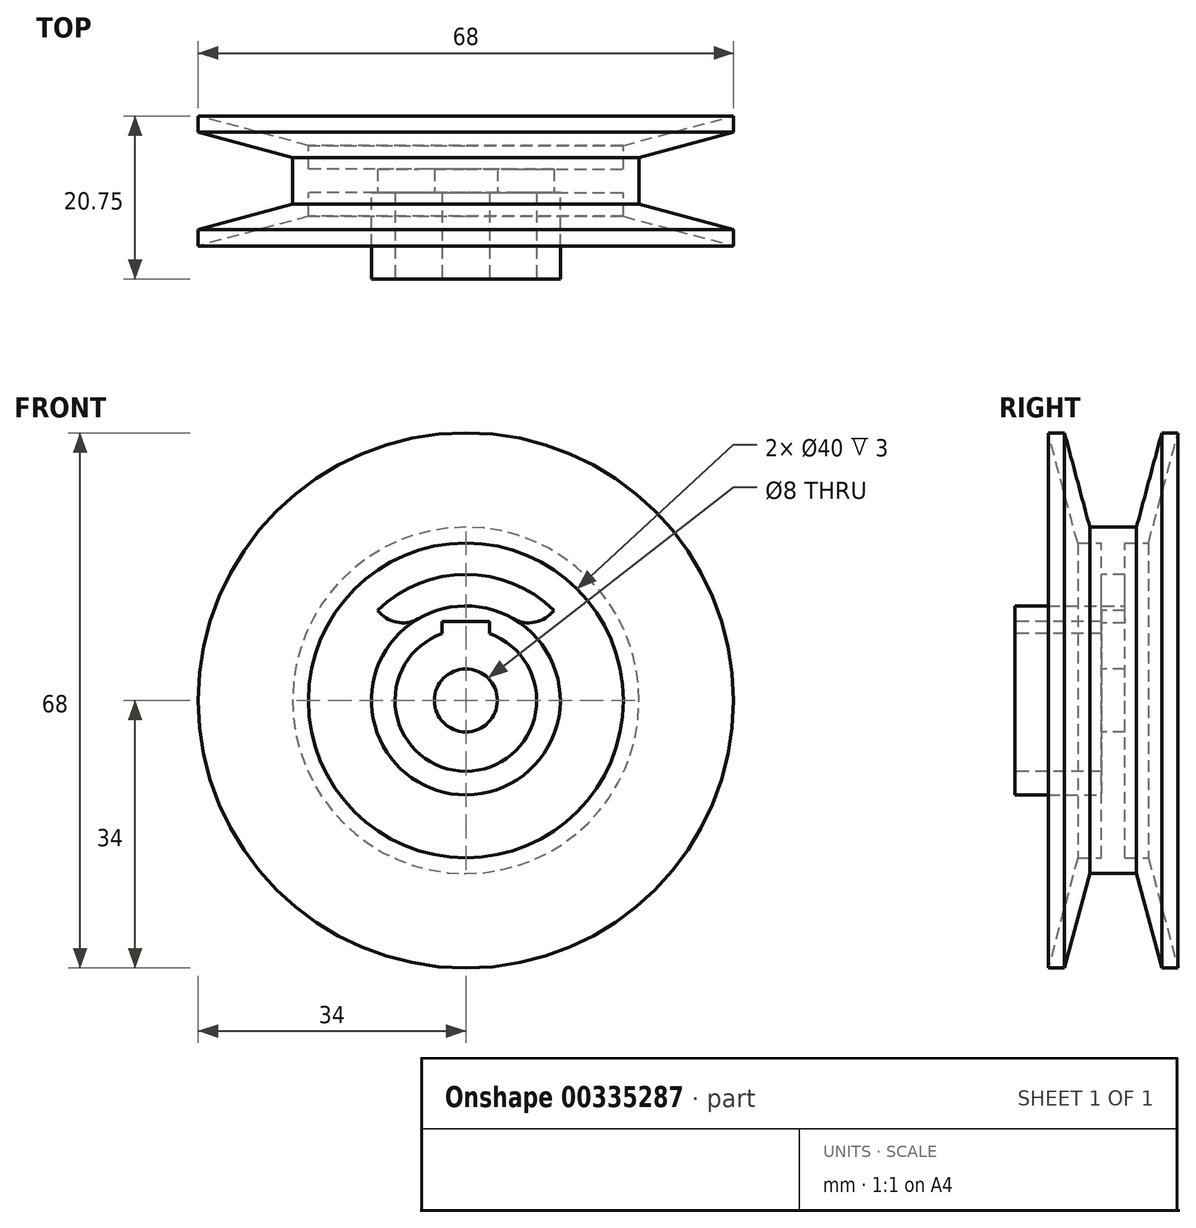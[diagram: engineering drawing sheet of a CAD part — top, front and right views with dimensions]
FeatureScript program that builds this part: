
annotation { "Feature Type Name" : "Feature", "Feature Type Description" : "" }
export const myFeature = defineFeature(function(context is Context, id is Id, definition is map)
    precondition{}
    {
        {
            var Q0;
            Q0=qCreatedBy(makeId("Front.planeOp"),FACE);
            var sketch = newSketch(context, id + "F0", { "sketchPlane" : qUnion([Q0])});
            skCircle(sketch, "E0", {"center": v(0, 0) * mm, "radius": 20 * mm});
            skSolve(sketch);
        }
        {
            var Q0;
            Q0=makeQuery(id+"F0.imprint","IMPRINT",FACE,{"disambiguationData":[TD([[makeQuery(id+"F0.imprint","IMPRINT",EDGE,{"derivedFrom":sQuery(id+"F0.wireOp",EDGE,"E0")}),1.0]])]});
            extrude(context, id + "F1", {"entities" : qUnion([Q0]), "depth" : 3 * mm, "symmetric" : true});
        }
        {
            var Q0;
            Q0=qCreatedBy(makeId("Right.planeOp"),FACE);
            var sketch = newSketch(context, id + "F2", { "sketchPlane" : qUnion([Q0])});
            skLineSegment(sketch, "E1", {"start": v(0, 20) * mm, "end": v(4.5, 20) * mm});
            skLineSegment(sketch, "E2", {"start": v(4.5, 20) * mm, "end": v(8.25, 34) * mm});
            skLineSegment(sketch, "E3.0", {"start": v(0, 22) * mm, "end": v(2.97, 22) * mm});
            skLineSegment(sketch, "E4.0", {"start": v(2.97, 22) * mm, "end": v(6.18, 34) * mm});
            skLineSegment(sketch, "E5", {"start": v(6.18, 34) * mm, "end": v(8.25, 34) * mm});
            skLineSegment(sketch, "E6", {"start": v(0, 20) * mm, "end": v(0, 22) * mm});
            skLineSegment(sketch, "E7.MirrorCS", {"start": v(0, 22) * mm, "end": v(-2.97, 22) * mm});
            skLineSegment(sketch, "E8.MirrorCS", {"start": v(-2.97, 22) * mm, "end": v(-6.18, 34) * mm});
            skLineSegment(sketch, "E9.MirrorCS", {"start": v(-6.18, 34) * mm, "end": v(-8.25, 34) * mm});
            skLineSegment(sketch, "E10.MirrorCS", {"start": v(-4.5, 20) * mm, "end": v(-8.25, 34) * mm});
            skLineSegment(sketch, "E11.MirrorCS", {"start": v(0, 20) * mm, "end": v(-4.5, 20) * mm});
            skSolve(sketch);
        }
        {
            var Q0;
            Q0 = qSketchRegion(id + "F2", true);
            var Q1;
            Q1=makeQuery(id+"F1.opExtrude","CAP_EDGE",EDGE,{"disambiguationData":[OSD([sQuery(id+"F0.wireOp",EDGE,"E0")])],"isStart":false});
            revolve(context, id + "F3", {"operationType" : NewBodyOperationType.ADD, "entities" : qUnion([Q0]), "axis" : qUnion([Q1]), "revolveType" : RevolveType.FULL});
        }
        {
            var Q0;
            Q0=makeQuery(id+"F1.opExtrude","CAP_FACE",FACE,{"disambiguationData":[OSD([sQuery(id+"F0.wireOp",EDGE,"E0")])],"isStart":false});
            var sketch = newSketch(context, id + "F4", { "sketchPlane" : qUnion([Q0])});
            skCircle(sketch, "E12", {"center": v(0, 0) * mm, "radius": 12 * mm});
            skSolve(sketch);
        }
        {
            var Q0;
            Q0=makeQuery(id+"F4.imprint","IMPRINT",FACE,{"disambiguationData":[TD([[makeQuery(id+"F4.imprint","IMPRINT",EDGE,{"derivedFrom":sQuery(id+"F4.wireOp",EDGE,"E12")}),1.0]])]});
            extrude(context, id + "F5", {"entities" : qUnion([Q0]), "operationType" : NewBodyOperationType.ADD, "depth" : 11 * mm});
        }
        {
            var Q0;
            Q0=makeQuery(id+"F5.opExtrude","CAP_FACE",FACE,{"disambiguationData":[OSD([sQuery(id+"F4.wireOp",EDGE,"E12")])],"isStart":false});
            var sketch = newSketch(context, id + "F6", { "sketchPlane" : qUnion([Q0])});
            skCircle(sketch, "E13", {"center": v(0, 0) * mm, "radius": 9 * mm});
            skSolve(sketch);
        }
        {
            var Q0;
            Q0=makeQuery(id+"F6.imprint","IMPRINT",FACE,{"disambiguationData":[TD([[makeQuery(id+"F6.imprint","IMPRINT",EDGE,{"derivedFrom":sQuery(id+"F6.wireOp",EDGE,"E13")}),1.0]])]});
            extrude(context, id + "F7", {"entities" : qUnion([Q0]), "operationType" : NewBodyOperationType.REMOVE, "oppositeDirection" : true, "depth" : 11 * mm});
        }
        {
            var Q0;
            Q0=makeQuery(id+"F7.boolean.opBoolean","COPY",FACE,{"derivedFrom":makeQuery(id+"F7.opExtrude","CAP_FACE",FACE,{"disambiguationData":[OSD([sQuery(id+"F6.wireOp",EDGE,"E13")])],"isStart":false})});
            var sketch = newSketch(context, id + "F8", { "sketchPlane" : qUnion([Q0])});
            skCircle(sketch, "E14", {"center": v(0, 0) * mm, "radius": 4 * mm});
            skSolve(sketch);
        }
        {
            var Q0;
            Q0=makeQuery(id+"F8.imprint","IMPRINT",FACE,{"disambiguationData":[TD([[makeQuery(id+"F8.imprint","IMPRINT",EDGE,{"derivedFrom":sQuery(id+"F8.wireOp",EDGE,"E14")}),1.0]])]});
            extrude(context, id + "F9", {"entities" : qUnion([Q0]), "operationType" : NewBodyOperationType.REMOVE, "oppositeDirection" : true, "depth" : 25 * mm});
        }
        {
            var Q0;
            Q0=makeQuery(id+"F5.opExtrude","CAP_FACE",FACE,{"disambiguationData":[OSD([sQuery(id+"F4.wireOp",EDGE,"E12")])],"isStart":false});
            var sketch = newSketch(context, id + "F10", { "sketchPlane" : qUnion([Q0])});
            skCircle(sketch, "E15.0", {"center": v(0, 0) * mm, "radius": 9 * mm});
            skLineSegment(sketch, "E16.bottom", {"start": v(3, 10) * mm, "end": v(-3, 10) * mm});
            skLineSegment(sketch, "E16.top", {"start": v(3, 8.49) * mm, "end": v(-3, 8.49) * mm});
            skLineSegment(sketch, "E16.left", {"start": v(3, 10) * mm, "end": v(3, 8.49) * mm});
            skLineSegment(sketch, "E16.right", {"start": v(-3, 10) * mm, "end": v(-3, 8.49) * mm});
            skPoint(sketch, "E16.middle", {"position": v(0, 9.24) * mm});
            skSolve(sketch);
        }
        {
            var Q0;
            Q0=makeQuery(id+"F10.imprint","IMPRINT",FACE,{"disambiguationData":[TD([[makeQuery(id+"F10.imprint","IMPRINT",EDGE,{"derivedFrom":sQuery(id+"F10.wireOp",EDGE,"E16.bottom")}),1.0]])]});
            var Q1;
            Q1=makeQuery(id+"F7.boolean.opBoolean","COPY",FACE,{"derivedFrom":makeQuery(id+"F7.opExtrude","CAP_FACE",FACE,{"disambiguationData":[OSD([sQuery(id+"F6.wireOp",EDGE,"E13")])],"isStart":false})});
            extrude(context, id + "F11", {"entities" : qUnion([Q0]), "operationType" : NewBodyOperationType.REMOVE, "endBound" : BoundingType.UP_TO_SURFACE, "oppositeDirection" : true, "endBoundEntityFace" : qUnion([Q1]), "depth" : 25 * mm});
        }
        {
            var Q0;
            Q0=makeQuery(id+"F1.opExtrude","CAP_FACE",FACE,{"disambiguationData":[OSD([sQuery(id+"F0.wireOp",EDGE,"E0")])],"isStart":false});
            var sketch = newSketch(context, id + "F12", { "sketchPlane" : qUnion([Q0])});
            skCircle(sketch, "E17", {"center": v(0, 0) * mm, "radius": 16 * mm});
            skLineSegment(sketch, "E18", {"start": v(0, 0) * mm, "end": v(-8, 13.86) * mm});
            skLineSegment(sketch, "E19", {"start": v(0, 0) * mm, "end": v(8, 13.86) * mm});
            skLineSegment(sketch, "E20", {"start": v(0, 0) * mm, "end": v(0, 21.78) * mm, "construction": true});
            skArc(sketch, "E21", {"start": v(-10, 17.32) * mm, "mid": v(-11.46, 11.86) * mm, "end": v(-6, 10.4) * mm});
            skArc(sketch, "E22", {"start": v(10, 17.32) * mm, "mid": v(11.46, 11.86) * mm, "end": v(6, 10.4) * mm});
            skArc(sketch, "E23", {"start": v(-6, 10.4) * mm, "mid": v(0, 12) * mm, "end": v(6, 10.4) * mm});
            skArc(sketch, "E24", {"start": v(-10, 17.32) * mm, "mid": v(0, 20) * mm, "end": v(10, 17.32) * mm});
            skSolve(sketch);
        }
        {
            var Q0;
            {var subQ0=sQuery(id+"F12.wireOp",EDGE,"E24");Q0=makeQuery(id+"F12.imprint","IMPRINT",FACE,{"disambiguationData":[TD([[makeQuery(id+"F12.imprint","IMPRINT",EDGE,{"derivedFrom":subQ0}),1.0]])]});}
            var Q1;
            {var subQ0=sQuery(id+"F12.wireOp",EDGE,"E18");var subQ1=sQuery(id+"F12.wireOp",EDGE,"E17");var subQ2=makeQuery(id+"F12.imprint","INTERSECT",VERTEX,{"derivedFrom":[subQ1,subQ0]});Q1=makeQuery(id+"F12.imprint","IMPRINT",FACE,{"disambiguationData":[TD([[makeQuery(id+"F12.imprint","IMPRINT",EDGE,{"disambiguationData":[TD([[subQ2,-1.0]])],"derivedFrom":subQ1}),1.0]])]});}
            var Q2;
            {var subQ5=sQuery(id+"F12.wireOp",EDGE,"E23");Q2=makeQuery(id+"F12.imprint","IMPRINT",FACE,{"disambiguationData":[TD([[makeQuery(id+"F12.imprint","IMPRINT",EDGE,{"derivedFrom":subQ5}),-1.0]])]});}
            var Q3;
            {var subQ0=sQuery(id+"F12.wireOp",EDGE,"E19");var subQ1=sQuery(id+"F12.wireOp",EDGE,"E17");var subQ2=makeQuery(id+"F12.imprint","INTERSECT",VERTEX,{"derivedFrom":[subQ1,subQ0]});Q3=makeQuery(id+"F12.imprint","IMPRINT",FACE,{"disambiguationData":[TD([[makeQuery(id+"F12.imprint","IMPRINT",EDGE,{"disambiguationData":[TD([[subQ2,1.0]])],"derivedFrom":subQ1}),1.0]])]});}
            extrude(context, id + "F13", {"entities" : qUnion([Q0, Q1, Q2, Q3]), "operationType" : NewBodyOperationType.REMOVE, "oppositeDirection" : true, "depth" : 25 * mm});
        }
    });
